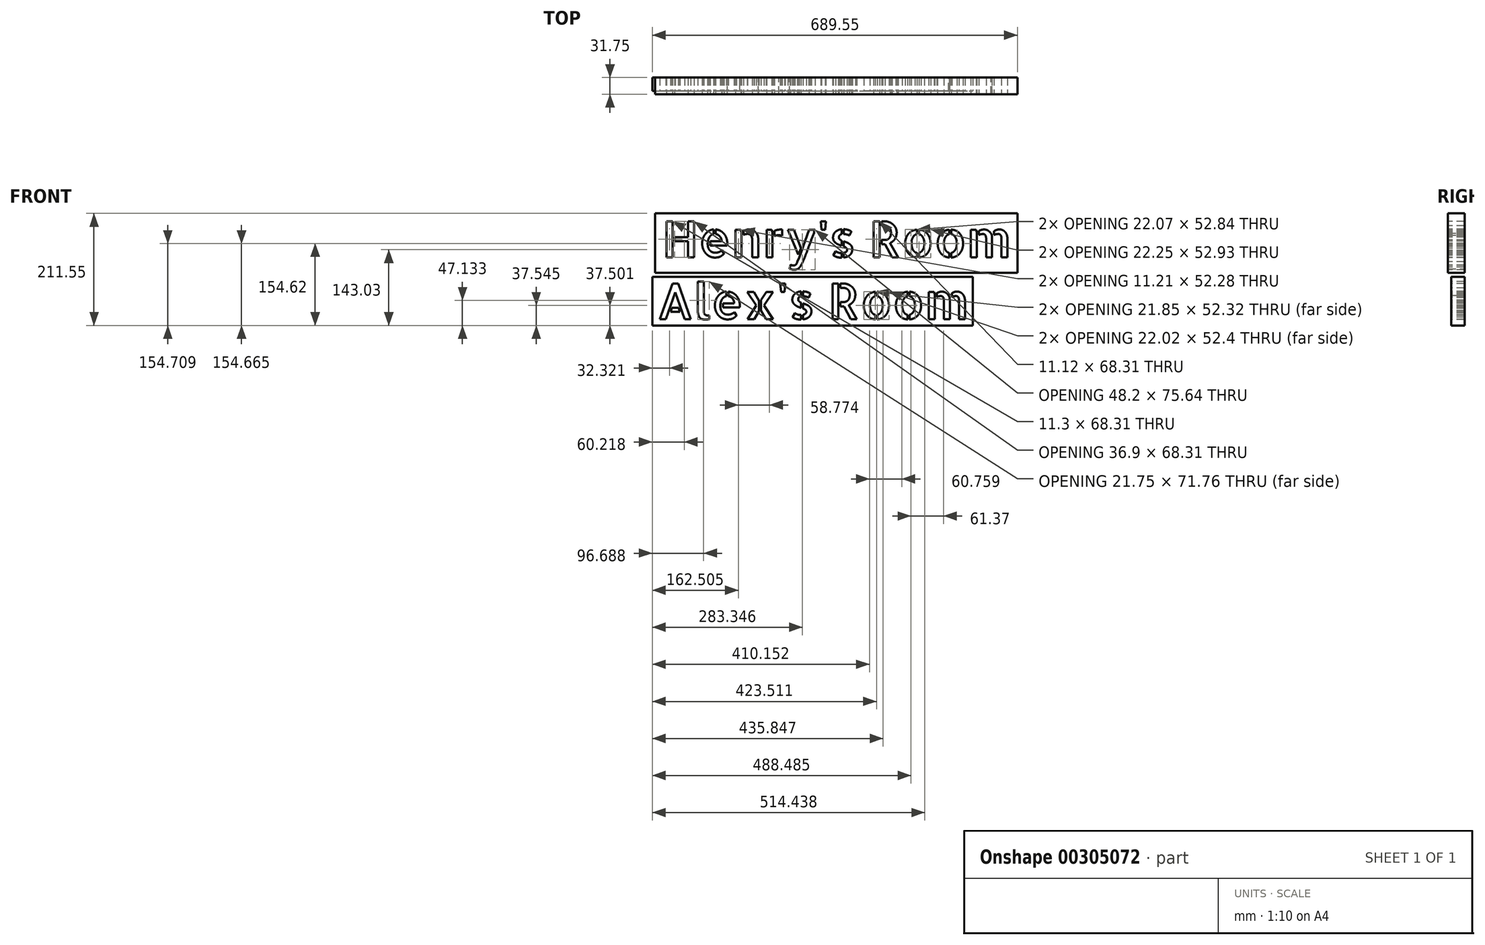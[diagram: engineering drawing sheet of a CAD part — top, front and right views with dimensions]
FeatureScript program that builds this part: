
annotation { "Feature Type Name" : "Feature", "Feature Type Description" : "" }
export const myFeature = defineFeature(function(context is Context, id is Id, definition is map)
    precondition{}
    {
        {
            var Q0;
            Q0=qCreatedBy(makeId("Front.planeOp"),FACE);
            var sketch = newSketch(context, id + "F0", { "sketchPlane" : qUnion([Q0])});
            skLineSegment(sketch, "E0.bottom", {"start": v(-190.62, -58.23) * mm, "end": v(414.55, -58.23) * mm});
            skLineSegment(sketch, "E0.top", {"start": v(-190.62, 33.33) * mm, "end": v(414.55, 33.33) * mm});
            skLineSegment(sketch, "E0.left", {"start": v(-190.62, -58.23) * mm, "end": v(-190.62, 33.33) * mm});
            skLineSegment(sketch, "E0.right", {"start": v(414.55, -58.23) * mm, "end": v(414.55, 33.33) * mm});
            skText(sketch, "E1", { "text": "Alex\'s Room", "fontName": "AllertaStencil-Regular.ttf"});
            const initialGuessF0  = {"E1": [-0.18217, -0.04652, 1, 0, 0.06766]};
            skSetInitialGuess(sketch, initialGuessF0);
            skSolve(sketch);
        }
        {
            var Q0;
            Q0 = qSketchRegion(id + "F0", true);
            extrude(context, id + "F1", {"entities" : qUnion([Q0]), "oppositeDirection" : true, "depth" : 25.4 * mm});
        }
        {
            var Q0;
            Q0=qCreatedBy(makeId("Front.planeOp"),FACE);
            var sketch = newSketch(context, id + "F2", { "sketchPlane" : qUnion([Q0])});
            skLineSegment(sketch, "E2.bottom", {"start": v(-185.58, 41.35) * mm, "end": v(498.93, 41.35) * mm});
            skLineSegment(sketch, "E2.top", {"start": v(-185.58, 153.32) * mm, "end": v(498.93, 153.32) * mm});
            skLineSegment(sketch, "E2.left", {"start": v(-185.58, 41.35) * mm, "end": v(-185.58, 153.32) * mm});
            skLineSegment(sketch, "E2.right", {"start": v(498.93, 41.35) * mm, "end": v(498.93, 153.32) * mm});
            skText(sketch, "E3", { "text": "Henry\'s Room", "fontName": "AllertaStencil-Regular.ttf"});
            const initialGuessF2  = {"E3": [-0.17267, 0.07034, 1, 0, 0.06834]};
            skSetInitialGuess(sketch, initialGuessF2);
            skSolve(sketch);
        }
        {
            var Q0;
            Q0 = qSketchRegion(id + "F2", true);
            extrude(context, id + "F3", {"entities" : qUnion([Q0]), "oppositeDirection" : true, "depth" : 25.4 * mm});
        }
        {
            var Q0;
            Q0=makeQuery(id+"F3.opExtrude","CAP_FACE",FACE,{"disambiguationData":[OSD([sQuery(id+"F2.wireOp",EDGE,"E2.bottom"),sQuery(id+"F2.wireOp",EDGE,"E2.top"),sQuery(id+"F2.wireOp",EDGE,"E2.left"),sQuery(id+"F2.wireOp",EDGE,"E2.right"),sQuery(id+"F2.wireOp",EDGE,"E3.sketch_text.stroke-0"),sQuery(id+"F2.wireOp",EDGE,"E3.sketch_text.stroke-1"),sQuery(id+"F2.wireOp",EDGE,"E3.sketch_text.stroke-2"),sQuery(id+"F2.wireOp",EDGE,"E3.sketch_text.stroke-3"),sQuery(id+"F2.wireOp",EDGE,"E3.sketch_text.stroke-4"),sQuery(id+"F2.wireOp",EDGE,"E3.sketch_text.stroke-5"),sQuery(id+"F2.wireOp",EDGE,"E3.sketch_text.stroke-6"),sQuery(id+"F2.wireOp",EDGE,"E3.sketch_text.stroke-7"),sQuery(id+"F2.wireOp",EDGE,"E3.sketch_text.stroke-8"),sQuery(id+"F2.wireOp",EDGE,"E3.sketch_text.stroke-9"),sQuery(id+"F2.wireOp",EDGE,"E3.sketch_text.stroke-10"),sQuery(id+"F2.wireOp",EDGE,"E3.sketch_text.stroke-11"),sQuery(id+"F2.wireOp",EDGE,"E3.sketch_text.stroke-12"),sQuery(id+"F2.wireOp",EDGE,"E3.sketch_text.stroke-13"),sQuery(id+"F2.wireOp",EDGE,"E3.sketch_text.stroke-14"),sQuery(id+"F2.wireOp",EDGE,"E3.sketch_text.stroke-15"),sQuery(id+"F2.wireOp",EDGE,"E3.sketch_text.stroke-16"),sQuery(id+"F2.wireOp",EDGE,"E3.sketch_text.stroke-17"),sQuery(id+"F2.wireOp",EDGE,"E3.sketch_text.stroke-18"),sQuery(id+"F2.wireOp",EDGE,"E3.sketch_text.stroke-19"),sQuery(id+"F2.wireOp",EDGE,"E3.sketch_text.stroke-20"),sQuery(id+"F2.wireOp",EDGE,"E3.sketch_text.stroke-21"),sQuery(id+"F2.wireOp",EDGE,"E3.sketch_text.stroke-22"),sQuery(id+"F2.wireOp",EDGE,"E3.sketch_text.stroke-23"),sQuery(id+"F2.wireOp",EDGE,"E3.sketch_text.stroke-24"),sQuery(id+"F2.wireOp",EDGE,"E3.sketch_text.stroke-25"),sQuery(id+"F2.wireOp",EDGE,"E3.sketch_text.stroke-26"),sQuery(id+"F2.wireOp",EDGE,"E3.sketch_text.stroke-27"),sQuery(id+"F2.wireOp",EDGE,"E3.sketch_text.stroke-28"),sQuery(id+"F2.wireOp",EDGE,"E3.sketch_text.stroke-29"),sQuery(id+"F2.wireOp",EDGE,"E3.sketch_text.stroke-30"),sQuery(id+"F2.wireOp",EDGE,"E3.sketch_text.stroke-31"),sQuery(id+"F2.wireOp",EDGE,"E3.sketch_text.stroke-32"),sQuery(id+"F2.wireOp",EDGE,"E3.sketch_text.stroke-33"),sQuery(id+"F2.wireOp",EDGE,"E3.sketch_text.stroke-34"),sQuery(id+"F2.wireOp",EDGE,"E3.sketch_text.stroke-35"),sQuery(id+"F2.wireOp",EDGE,"E3.sketch_text.stroke-36"),sQuery(id+"F2.wireOp",EDGE,"E3.sketch_text.stroke-37"),sQuery(id+"F2.wireOp",EDGE,"E3.sketch_text.stroke-38"),sQuery(id+"F2.wireOp",EDGE,"E3.sketch_text.stroke-39"),sQuery(id+"F2.wireOp",EDGE,"E3.sketch_text.stroke-40"),sQuery(id+"F2.wireOp",EDGE,"E3.sketch_text.stroke-41"),sQuery(id+"F2.wireOp",EDGE,"E3.sketch_text.stroke-42"),sQuery(id+"F2.wireOp",EDGE,"E3.sketch_text.stroke-43"),sQuery(id+"F2.wireOp",EDGE,"E3.sketch_text.stroke-44"),sQuery(id+"F2.wireOp",EDGE,"E3.sketch_text.stroke-45"),sQuery(id+"F2.wireOp",EDGE,"E3.sketch_text.stroke-46"),sQuery(id+"F2.wireOp",EDGE,"E3.sketch_text.stroke-47"),sQuery(id+"F2.wireOp",EDGE,"E3.sketch_text.stroke-48"),sQuery(id+"F2.wireOp",EDGE,"E3.sketch_text.stroke-49"),sQuery(id+"F2.wireOp",EDGE,"E3.sketch_text.stroke-50"),sQuery(id+"F2.wireOp",EDGE,"E3.sketch_text.stroke-51"),sQuery(id+"F2.wireOp",EDGE,"E3.sketch_text.stroke-52"),sQuery(id+"F2.wireOp",EDGE,"E3.sketch_text.stroke-53"),sQuery(id+"F2.wireOp",EDGE,"E3.sketch_text.stroke-54"),sQuery(id+"F2.wireOp",EDGE,"E3.sketch_text.stroke-55"),sQuery(id+"F2.wireOp",EDGE,"E3.sketch_text.stroke-56"),sQuery(id+"F2.wireOp",EDGE,"E3.sketch_text.stroke-57"),sQuery(id+"F2.wireOp",EDGE,"E3.sketch_text.stroke-58"),sQuery(id+"F2.wireOp",EDGE,"E3.sketch_text.stroke-59"),sQuery(id+"F2.wireOp",EDGE,"E3.sketch_text.stroke-60"),sQuery(id+"F2.wireOp",EDGE,"E3.sketch_text.stroke-61"),sQuery(id+"F2.wireOp",EDGE,"E3.sketch_text.stroke-62"),sQuery(id+"F2.wireOp",EDGE,"E3.sketch_text.stroke-63"),sQuery(id+"F2.wireOp",EDGE,"E3.sketch_text.stroke-64"),sQuery(id+"F2.wireOp",EDGE,"E3.sketch_text.stroke-65"),sQuery(id+"F2.wireOp",EDGE,"E3.sketch_text.stroke-66"),sQuery(id+"F2.wireOp",EDGE,"E3.sketch_text.stroke-67"),sQuery(id+"F2.wireOp",EDGE,"E3.sketch_text.stroke-68"),sQuery(id+"F2.wireOp",EDGE,"E3.sketch_text.stroke-69"),sQuery(id+"F2.wireOp",EDGE,"E3.sketch_text.stroke-70"),sQuery(id+"F2.wireOp",EDGE,"E3.sketch_text.stroke-71"),sQuery(id+"F2.wireOp",EDGE,"E3.sketch_text.stroke-72"),sQuery(id+"F2.wireOp",EDGE,"E3.sketch_text.stroke-73"),sQuery(id+"F2.wireOp",EDGE,"E3.sketch_text.stroke-74"),sQuery(id+"F2.wireOp",EDGE,"E3.sketch_text.stroke-75"),sQuery(id+"F2.wireOp",EDGE,"E3.sketch_text.stroke-76"),sQuery(id+"F2.wireOp",EDGE,"E3.sketch_text.stroke-77"),sQuery(id+"F2.wireOp",EDGE,"E3.sketch_text.stroke-78"),sQuery(id+"F2.wireOp",EDGE,"E3.sketch_text.stroke-79"),sQuery(id+"F2.wireOp",EDGE,"E3.sketch_text.stroke-80"),sQuery(id+"F2.wireOp",EDGE,"E3.sketch_text.stroke-81"),sQuery(id+"F2.wireOp",EDGE,"E3.sketch_text.stroke-82"),sQuery(id+"F2.wireOp",EDGE,"E3.sketch_text.stroke-83"),sQuery(id+"F2.wireOp",EDGE,"E3.sketch_text.stroke-84"),sQuery(id+"F2.wireOp",EDGE,"E3.sketch_text.stroke-85"),sQuery(id+"F2.wireOp",EDGE,"E3.sketch_text.stroke-86"),sQuery(id+"F2.wireOp",EDGE,"E3.sketch_text.stroke-87"),sQuery(id+"F2.wireOp",EDGE,"E3.sketch_text.stroke-88"),sQuery(id+"F2.wireOp",EDGE,"E3.sketch_text.stroke-89"),sQuery(id+"F2.wireOp",EDGE,"E3.sketch_text.stroke-90"),sQuery(id+"F2.wireOp",EDGE,"E3.sketch_text.stroke-91"),sQuery(id+"F2.wireOp",EDGE,"E3.sketch_text.stroke-92"),sQuery(id+"F2.wireOp",EDGE,"E3.sketch_text.stroke-93"),sQuery(id+"F2.wireOp",EDGE,"E3.sketch_text.stroke-94"),sQuery(id+"F2.wireOp",EDGE,"E3.sketch_text.stroke-95"),sQuery(id+"F2.wireOp",EDGE,"E3.sketch_text.stroke-96"),sQuery(id+"F2.wireOp",EDGE,"E3.sketch_text.stroke-97"),sQuery(id+"F2.wireOp",EDGE,"E3.sketch_text.stroke-98"),sQuery(id+"F2.wireOp",EDGE,"E3.sketch_text.stroke-99"),sQuery(id+"F2.wireOp",EDGE,"E3.sketch_text.stroke-100"),sQuery(id+"F2.wireOp",EDGE,"E3.sketch_text.stroke-101"),sQuery(id+"F2.wireOp",EDGE,"E3.sketch_text.stroke-102"),sQuery(id+"F2.wireOp",EDGE,"E3.sketch_text.stroke-103"),sQuery(id+"F2.wireOp",EDGE,"E3.sketch_text.stroke-104"),sQuery(id+"F2.wireOp",EDGE,"E3.sketch_text.stroke-105"),sQuery(id+"F2.wireOp",EDGE,"E3.sketch_text.stroke-106"),sQuery(id+"F2.wireOp",EDGE,"E3.sketch_text.stroke-107"),sQuery(id+"F2.wireOp",EDGE,"E3.sketch_text.stroke-108"),sQuery(id+"F2.wireOp",EDGE,"E3.sketch_text.stroke-109"),sQuery(id+"F2.wireOp",EDGE,"E3.sketch_text.stroke-110"),sQuery(id+"F2.wireOp",EDGE,"E3.sketch_text.stroke-111"),sQuery(id+"F2.wireOp",EDGE,"E3.sketch_text.stroke-112"),sQuery(id+"F2.wireOp",EDGE,"E3.sketch_text.stroke-113"),sQuery(id+"F2.wireOp",EDGE,"E3.sketch_text.stroke-114"),sQuery(id+"F2.wireOp",EDGE,"E3.sketch_text.stroke-115"),sQuery(id+"F2.wireOp",EDGE,"E3.sketch_text.stroke-116"),sQuery(id+"F2.wireOp",EDGE,"E3.sketch_text.stroke-117"),sQuery(id+"F2.wireOp",EDGE,"E3.sketch_text.stroke-118"),sQuery(id+"F2.wireOp",EDGE,"E3.sketch_text.stroke-119"),sQuery(id+"F2.wireOp",EDGE,"E3.sketch_text.stroke-120"),sQuery(id+"F2.wireOp",EDGE,"E3.sketch_text.stroke-121"),sQuery(id+"F2.wireOp",EDGE,"E3.sketch_text.stroke-122"),sQuery(id+"F2.wireOp",EDGE,"E3.sketch_text.stroke-123"),sQuery(id+"F2.wireOp",EDGE,"E3.sketch_text.stroke-124"),sQuery(id+"F2.wireOp",EDGE,"E3.sketch_text.stroke-125"),sQuery(id+"F2.wireOp",EDGE,"E3.sketch_text.stroke-126"),sQuery(id+"F2.wireOp",EDGE,"E3.sketch_text.stroke-127"),sQuery(id+"F2.wireOp",EDGE,"E3.sketch_text.stroke-128"),sQuery(id+"F2.wireOp",EDGE,"E3.sketch_text.stroke-129"),sQuery(id+"F2.wireOp",EDGE,"E3.sketch_text.stroke-130"),sQuery(id+"F2.wireOp",EDGE,"E3.sketch_text.stroke-131"),sQuery(id+"F2.wireOp",EDGE,"E3.sketch_text.stroke-132"),sQuery(id+"F2.wireOp",EDGE,"E3.sketch_text.stroke-133"),sQuery(id+"F2.wireOp",EDGE,"E3.sketch_text.stroke-134"),sQuery(id+"F2.wireOp",EDGE,"E3.sketch_text.stroke-135"),sQuery(id+"F2.wireOp",EDGE,"E3.sketch_text.stroke-136"),sQuery(id+"F2.wireOp",EDGE,"E3.sketch_text.stroke-137"),sQuery(id+"F2.wireOp",EDGE,"E3.sketch_text.stroke-138"),sQuery(id+"F2.wireOp",EDGE,"E3.sketch_text.stroke-139"),sQuery(id+"F2.wireOp",EDGE,"E3.sketch_text.stroke-140"),sQuery(id+"F2.wireOp",EDGE,"E3.sketch_text.stroke-141"),sQuery(id+"F2.wireOp",EDGE,"E3.sketch_text.stroke-142"),sQuery(id+"F2.wireOp",EDGE,"E3.sketch_text.stroke-143"),sQuery(id+"F2.wireOp",EDGE,"E3.sketch_text.stroke-144"),sQuery(id+"F2.wireOp",EDGE,"E3.sketch_text.stroke-145"),sQuery(id+"F2.wireOp",EDGE,"E3.sketch_text.stroke-146"),sQuery(id+"F2.wireOp",EDGE,"E3.sketch_text.stroke-147"),sQuery(id+"F2.wireOp",EDGE,"E3.sketch_text.stroke-148"),sQuery(id+"F2.wireOp",EDGE,"E3.sketch_text.stroke-149"),sQuery(id+"F2.wireOp",EDGE,"E3.sketch_text.stroke-150"),sQuery(id+"F2.wireOp",EDGE,"E3.sketch_text.stroke-151"),sQuery(id+"F2.wireOp",EDGE,"E3.sketch_text.stroke-152"),sQuery(id+"F2.wireOp",EDGE,"E3.sketch_text.stroke-153"),sQuery(id+"F2.wireOp",EDGE,"E3.sketch_text.stroke-154"),sQuery(id+"F2.wireOp",EDGE,"E3.sketch_text.stroke-155"),sQuery(id+"F2.wireOp",EDGE,"E3.sketch_text.stroke-156"),sQuery(id+"F2.wireOp",EDGE,"E3.sketch_text.stroke-157"),sQuery(id+"F2.wireOp",EDGE,"E3.sketch_text.stroke-158"),sQuery(id+"F2.wireOp",EDGE,"E3.sketch_text.stroke-159"),sQuery(id+"F2.wireOp",EDGE,"E3.sketch_text.stroke-160"),sQuery(id+"F2.wireOp",EDGE,"E3.sketch_text.stroke-161"),sQuery(id+"F2.wireOp",EDGE,"E3.sketch_text.stroke-162"),sQuery(id+"F2.wireOp",EDGE,"E3.sketch_text.stroke-163"),sQuery(id+"F2.wireOp",EDGE,"E3.sketch_text.stroke-164"),sQuery(id+"F2.wireOp",EDGE,"E3.sketch_text.stroke-165"),sQuery(id+"F2.wireOp",EDGE,"E3.sketch_text.stroke-166"),sQuery(id+"F2.wireOp",EDGE,"E3.sketch_text.stroke-167"),sQuery(id+"F2.wireOp",EDGE,"E3.sketch_text.stroke-168"),sQuery(id+"F2.wireOp",EDGE,"E3.sketch_text.stroke-169"),sQuery(id+"F2.wireOp",EDGE,"E3.sketch_text.stroke-170"),sQuery(id+"F2.wireOp",EDGE,"E3.sketch_text.stroke-171"),sQuery(id+"F2.wireOp",EDGE,"E3.sketch_text.stroke-172"),sQuery(id+"F2.wireOp",EDGE,"E3.sketch_text.stroke-173"),sQuery(id+"F2.wireOp",EDGE,"E3.sketch_text.stroke-174"),sQuery(id+"F2.wireOp",EDGE,"E3.sketch_text.stroke-175"),sQuery(id+"F2.wireOp",EDGE,"E3.sketch_text.stroke-176"),sQuery(id+"F2.wireOp",EDGE,"E3.sketch_text.stroke-177"),sQuery(id+"F2.wireOp",EDGE,"E3.sketch_text.stroke-178"),sQuery(id+"F2.wireOp",EDGE,"E3.sketch_text.stroke-179"),sQuery(id+"F2.wireOp",EDGE,"E3.sketch_text.stroke-180"),sQuery(id+"F2.wireOp",EDGE,"E3.sketch_text.stroke-181"),sQuery(id+"F2.wireOp",EDGE,"E3.sketch_text.stroke-182"),sQuery(id+"F2.wireOp",EDGE,"E3.sketch_text.stroke-183"),sQuery(id+"F2.wireOp",EDGE,"E3.sketch_text.stroke-184"),sQuery(id+"F2.wireOp",EDGE,"E3.sketch_text.stroke-185"),sQuery(id+"F2.wireOp",EDGE,"E3.sketch_text.stroke-186"),sQuery(id+"F2.wireOp",EDGE,"E3.sketch_text.stroke-187"),sQuery(id+"F2.wireOp",EDGE,"E3.sketch_text.stroke-188"),sQuery(id+"F2.wireOp",EDGE,"E3.sketch_text.stroke-189"),sQuery(id+"F2.wireOp",EDGE,"E3.sketch_text.stroke-190"),sQuery(id+"F2.wireOp",EDGE,"E3.sketch_text.stroke-191"),sQuery(id+"F2.wireOp",EDGE,"E3.sketch_text.stroke-192"),sQuery(id+"F2.wireOp",EDGE,"E3.sketch_text.stroke-193"),sQuery(id+"F2.wireOp",EDGE,"E3.sketch_text.stroke-194"),sQuery(id+"F2.wireOp",EDGE,"E3.sketch_text.stroke-195"),sQuery(id+"F2.wireOp",EDGE,"E3.sketch_text.stroke-196"),sQuery(id+"F2.wireOp",EDGE,"E3.sketch_text.stroke-197"),sQuery(id+"F2.wireOp",EDGE,"E3.sketch_text.stroke-198"),sQuery(id+"F2.wireOp",EDGE,"E3.sketch_text.stroke-199"),sQuery(id+"F2.wireOp",EDGE,"E3.sketch_text.stroke-200"),sQuery(id+"F2.wireOp",EDGE,"E3.sketch_text.stroke-201"),sQuery(id+"F2.wireOp",EDGE,"E3.sketch_text.stroke-202"),sQuery(id+"F2.wireOp",EDGE,"E3.sketch_text.stroke-203"),sQuery(id+"F2.wireOp",EDGE,"E3.sketch_text.stroke-204"),sQuery(id+"F2.wireOp",EDGE,"E3.sketch_text.stroke-205"),sQuery(id+"F2.wireOp",EDGE,"E3.sketch_text.stroke-206"),sQuery(id+"F2.wireOp",EDGE,"E3.sketch_text.stroke-207"),sQuery(id+"F2.wireOp",EDGE,"E3.sketch_text.stroke-208"),sQuery(id+"F2.wireOp",EDGE,"E3.sketch_text.stroke-209"),sQuery(id+"F2.wireOp",EDGE,"E3.sketch_text.stroke-210"),sQuery(id+"F2.wireOp",EDGE,"E3.sketch_text.stroke-211"),sQuery(id+"F2.wireOp",EDGE,"E3.sketch_text.stroke-212"),sQuery(id+"F2.wireOp",EDGE,"E3.sketch_text.stroke-213"),sQuery(id+"F2.wireOp",EDGE,"E3.sketch_text.stroke-214"),sQuery(id+"F2.wireOp",EDGE,"E3.sketch_text.stroke-215"),sQuery(id+"F2.wireOp",EDGE,"E3.sketch_text.stroke-216"),sQuery(id+"F2.wireOp",EDGE,"E3.sketch_text.stroke-217"),sQuery(id+"F2.wireOp",EDGE,"E3.sketch_text.stroke-218"),sQuery(id+"F2.wireOp",EDGE,"E3.sketch_text.stroke-219"),sQuery(id+"F2.wireOp",EDGE,"E3.sketch_text.stroke-220"),sQuery(id+"F2.wireOp",EDGE,"E3.sketch_text.stroke-221"),sQuery(id+"F2.wireOp",EDGE,"E3.sketch_text.stroke-222"),sQuery(id+"F2.wireOp",EDGE,"E3.sketch_text.stroke-223"),sQuery(id+"F2.wireOp",EDGE,"E3.sketch_text.stroke-224"),sQuery(id+"F2.wireOp",EDGE,"E3.sketch_text.stroke-225"),sQuery(id+"F2.wireOp",EDGE,"E3.sketch_text.stroke-226"),sQuery(id+"F2.wireOp",EDGE,"E3.sketch_text.stroke-227"),sQuery(id+"F2.wireOp",EDGE,"E3.sketch_text.stroke-228"),sQuery(id+"F2.wireOp",EDGE,"E3.sketch_text.stroke-229"),sQuery(id+"F2.wireOp",EDGE,"E3.sketch_text.stroke-230"),sQuery(id+"F2.wireOp",EDGE,"E3.sketch_text.stroke-231"),sQuery(id+"F2.wireOp",EDGE,"E3.sketch_text.stroke-232"),sQuery(id+"F2.wireOp",EDGE,"E3.sketch_text.stroke-233"),sQuery(id+"F2.wireOp",EDGE,"E3.sketch_text.stroke-234"),sQuery(id+"F2.wireOp",EDGE,"E3.sketch_text.stroke-235"),sQuery(id+"F2.wireOp",EDGE,"E3.sketch_text.stroke-236"),sQuery(id+"F2.wireOp",EDGE,"E3.sketch_text.stroke-237"),sQuery(id+"F2.wireOp",EDGE,"E3.sketch_text.stroke-238"),sQuery(id+"F2.wireOp",EDGE,"E3.sketch_text.stroke-239"),sQuery(id+"F2.wireOp",EDGE,"E3.sketch_text.stroke-240"),sQuery(id+"F2.wireOp",EDGE,"E3.sketch_text.stroke-241"),sQuery(id+"F2.wireOp",EDGE,"E3.sketch_text.stroke-242"),sQuery(id+"F2.wireOp",EDGE,"E3.sketch_text.stroke-243"),sQuery(id+"F2.wireOp",EDGE,"E3.sketch_text.stroke-244"),sQuery(id+"F2.wireOp",EDGE,"E3.sketch_text.stroke-245"),sQuery(id+"F2.wireOp",EDGE,"E3.sketch_text.stroke-246"),sQuery(id+"F2.wireOp",EDGE,"E3.sketch_text.stroke-247"),sQuery(id+"F2.wireOp",EDGE,"E3.sketch_text.stroke-248"),sQuery(id+"F2.wireOp",EDGE,"E3.sketch_text.stroke-249"),sQuery(id+"F2.wireOp",EDGE,"E3.sketch_text.stroke-250"),sQuery(id+"F2.wireOp",EDGE,"E3.sketch_text.stroke-251"),sQuery(id+"F2.wireOp",EDGE,"E3.sketch_text.stroke-252"),sQuery(id+"F2.wireOp",EDGE,"E3.sketch_text.stroke-253"),sQuery(id+"F2.wireOp",EDGE,"E3.sketch_text.stroke-254"),sQuery(id+"F2.wireOp",EDGE,"E3.sketch_text.stroke-255"),sQuery(id+"F2.wireOp",EDGE,"E3.sketch_text.stroke-256"),sQuery(id+"F2.wireOp",EDGE,"E3.sketch_text.stroke-257"),sQuery(id+"F2.wireOp",EDGE,"E3.sketch_text.stroke-258"),sQuery(id+"F2.wireOp",EDGE,"E3.sketch_text.stroke-259"),sQuery(id+"F2.wireOp",EDGE,"E3.sketch_text.stroke-260"),sQuery(id+"F2.wireOp",EDGE,"E3.sketch_text.stroke-261"),sQuery(id+"F2.wireOp",EDGE,"E3.sketch_text.stroke-262"),sQuery(id+"F2.wireOp",EDGE,"E3.sketch_text.stroke-263"),sQuery(id+"F2.wireOp",EDGE,"E3.sketch_text.stroke-264"),sQuery(id+"F2.wireOp",EDGE,"E3.sketch_text.stroke-265"),sQuery(id+"F2.wireOp",EDGE,"E3.sketch_text.stroke-266"),sQuery(id+"F2.wireOp",EDGE,"E3.sketch_text.stroke-267"),sQuery(id+"F2.wireOp",EDGE,"E3.sketch_text.stroke-268"),sQuery(id+"F2.wireOp",EDGE,"E3.sketch_text.stroke-269"),sQuery(id+"F2.wireOp",EDGE,"E3.sketch_text.stroke-270"),sQuery(id+"F2.wireOp",EDGE,"E3.sketch_text.stroke-271"),sQuery(id+"F2.wireOp",EDGE,"E3.sketch_text.stroke-272"),sQuery(id+"F2.wireOp",EDGE,"E3.sketch_text.stroke-273"),sQuery(id+"F2.wireOp",EDGE,"E3.sketch_text.stroke-274"),sQuery(id+"F2.wireOp",EDGE,"E3.sketch_text.stroke-275"),sQuery(id+"F2.wireOp",EDGE,"E3.sketch_text.stroke-276"),sQuery(id+"F2.wireOp",EDGE,"E3.sketch_text.stroke-277"),sQuery(id+"F2.wireOp",EDGE,"E3.sketch_text.stroke-278"),sQuery(id+"F2.wireOp",EDGE,"E3.sketch_text.stroke-279"),sQuery(id+"F2.wireOp",EDGE,"E3.sketch_text.stroke-280"),sQuery(id+"F2.wireOp",EDGE,"E3.sketch_text.stroke-281"),sQuery(id+"F2.wireOp",EDGE,"E3.sketch_text.stroke-282"),sQuery(id+"F2.wireOp",EDGE,"E3.sketch_text.stroke-283"),sQuery(id+"F2.wireOp",EDGE,"E3.sketch_text.stroke-284"),sQuery(id+"F2.wireOp",EDGE,"E3.sketch_text.stroke-285"),sQuery(id+"F2.wireOp",EDGE,"E3.sketch_text.stroke-286"),sQuery(id+"F2.wireOp",EDGE,"E3.sketch_text.stroke-287"),sQuery(id+"F2.wireOp",EDGE,"E3.sketch_text.stroke-288"),sQuery(id+"F2.wireOp",EDGE,"E3.sketch_text.stroke-289"),sQuery(id+"F2.wireOp",EDGE,"E3.sketch_text.stroke-290"),sQuery(id+"F2.wireOp",EDGE,"E3.sketch_text.stroke-291"),sQuery(id+"F2.wireOp",EDGE,"E3.sketch_text.stroke-292"),sQuery(id+"F2.wireOp",EDGE,"E3.sketch_text.stroke-293"),sQuery(id+"F2.wireOp",EDGE,"E3.sketch_text.stroke-294"),sQuery(id+"F2.wireOp",EDGE,"E3.sketch_text.stroke-295")])],"isStart":true});
            extrude(context, id + "F4", {"entities" : qUnion([Q0]), "operationType" : NewBodyOperationType.ADD, "depth" : 6.35 * mm});
        }
    });
